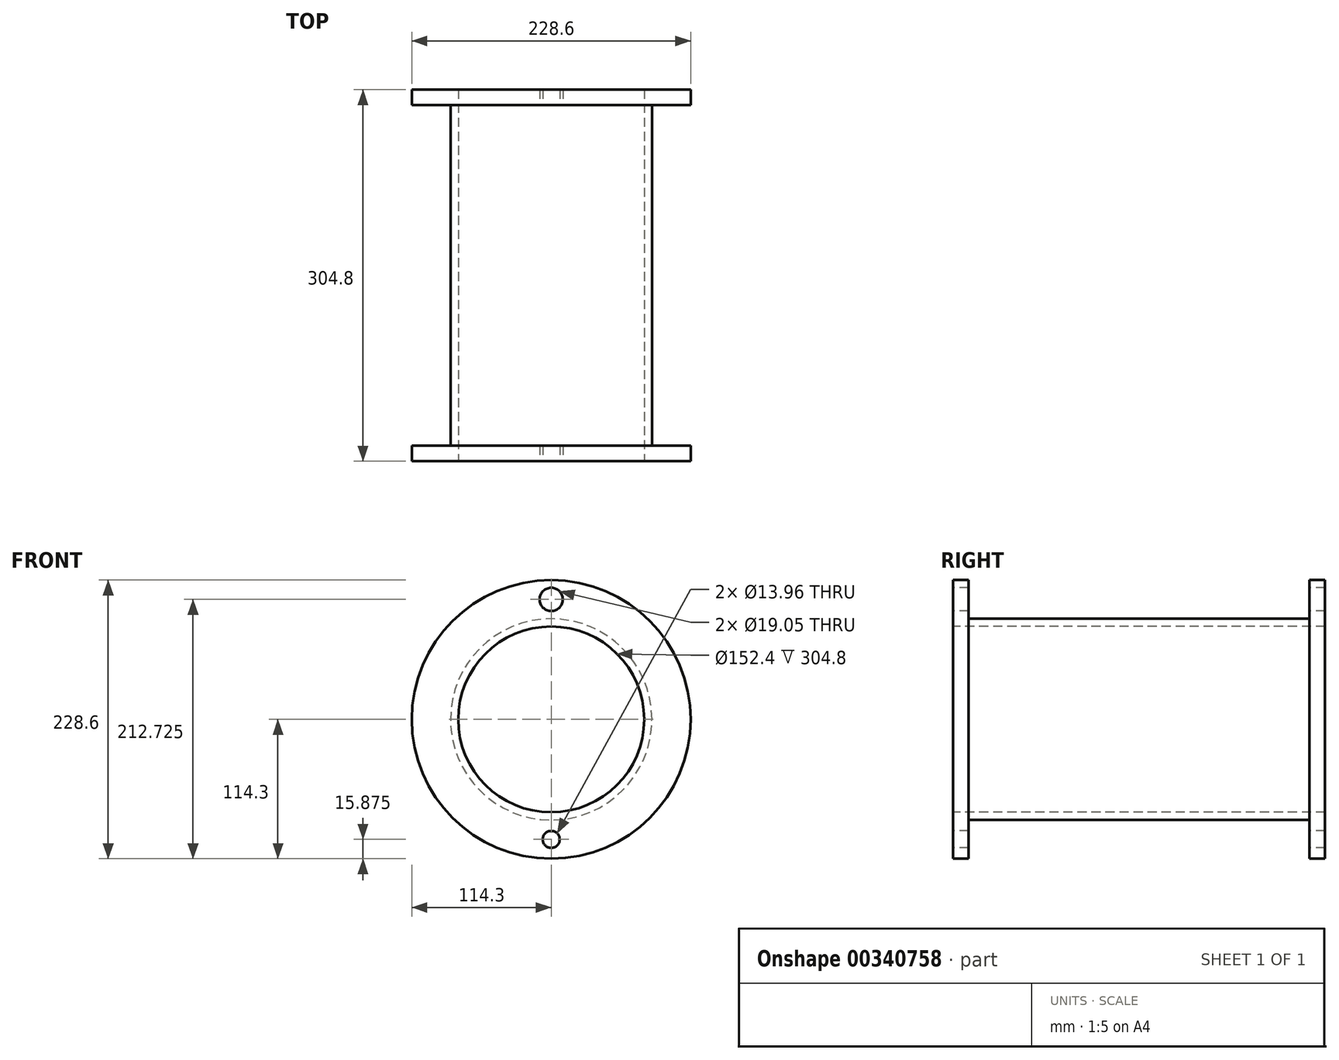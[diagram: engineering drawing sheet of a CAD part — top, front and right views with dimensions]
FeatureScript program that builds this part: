
annotation { "Feature Type Name" : "Feature", "Feature Type Description" : "" }
export const myFeature = defineFeature(function(context is Context, id is Id, definition is map)
    precondition{}
    {
        {
            var Q0;
            Q0=qCreatedBy(makeId("Right.planeOp"),FACE);
            var sketch = newSketch(context, id + "F0", { "sketchPlane" : qUnion([Q0])});
            skLineSegment(sketch, "E0", {"start": v(-372.41, 0) * mm, "end": v(512.39, 0) * mm, "construction": true});
            skLineSegment(sketch, "E1", {"start": v(0, 114.3) * mm, "end": v(-12.7, 114.3) * mm});
            skLineSegment(sketch, "E2", {"start": v(-12.7, 114.3) * mm, "end": v(-12.7, 82.55) * mm});
            skLineSegment(sketch, "E3", {"start": v(-12.7, 82.55) * mm, "end": v(-292.1, 82.55) * mm});
            skLineSegment(sketch, "E4", {"start": v(-292.1, 82.55) * mm, "end": v(-292.1, 114.3) * mm});
            skLineSegment(sketch, "E5", {"start": v(-292.1, 114.3) * mm, "end": v(-304.8, 114.3) * mm});
            skLineSegment(sketch, "E6", {"start": v(-304.8, 76.2) * mm, "end": v(0, 76.2) * mm});
            skLineSegment(sketch, "E7", {"start": v(-304.8, 114.3) * mm, "end": v(-304.8, 76.2) * mm});
            skLineSegment(sketch, "E8", {"start": v(0, 114.3) * mm, "end": v(0, 76.2) * mm});
            skSolve(sketch);
        }
        {
            var Q0;
            Q0=makeQuery(id+"F0.imprint","IMPRINT",FACE,{"disambiguationData":[TD([[makeQuery(id+"F0.imprint","IMPRINT",EDGE,{"derivedFrom":sQuery(id+"F0.wireOp",EDGE,"E1")}),1.0]])]});
            var Q1;
            Q1=sQuery(id+"F0.wireOp",EDGE,"E0");
            revolve(context, id + "F1", {"entities" : qUnion([Q0]), "axis" : qUnion([Q1]), "revolveType" : RevolveType.FULL});
        }
        {
            var Q0;
            Q0=makeQuery(id+"F1.opRevolve","SWEPT_FACE",FACE,{"disambiguationData":[OSD([sQuery(id+"F0.wireOp",EDGE,"E7")])]});
            cPlane(context, id + "F2", {"entities" : qUnion([Q0]), "cplaneType" : CPlaneType.OFFSET, "offset" : 0 * mm, "width" : 152.4 * mm, "height" : 152.4 * mm});
        }
        {
            var Q0;
            Q0=qCreatedBy(id+"F2.planeOp",FACE);
            var sketch = newSketch(context, id + "F3", { "sketchPlane" : qUnion([Q0])});
            skCircle(sketch, "E9", {"center": v(0, 0) * mm, "radius": 98.43 * mm, "construction": true});
            skCircle(sketch, "E10", {"center": v(0, 98.43) * mm, "radius": 9.53 * mm, "construction": true});
            skCircle(sketch, "E11.1.0", {"center": v(-69.6, 69.6) * mm, "radius": 9.53 * mm, "construction": true});
            skCircle(sketch, "E11.2.0", {"center": v(-98.43, 0) * mm, "radius": 9.53 * mm, "construction": true});
            skCircle(sketch, "E11.3.0", {"center": v(-69.6, -69.6) * mm, "radius": 9.53 * mm, "construction": true});
            skCircle(sketch, "E11.4.0", {"center": v(0, -98.43) * mm, "radius": 9.53 * mm, "construction": true});
            skCircle(sketch, "E11.5.0", {"center": v(69.6, -69.6) * mm, "radius": 9.53 * mm, "construction": true});
            skCircle(sketch, "E11.6.0", {"center": v(98.43, 0) * mm, "radius": 9.53 * mm, "construction": true});
            skCircle(sketch, "E11.7.0", {"center": v(69.6, 69.6) * mm, "radius": 9.53 * mm, "construction": true});
            skCircle(sketch, "E12", {"center": v(0, 98.43) * mm, "radius": 9.53 * mm});
            skCircle(sketch, "E13", {"center": v(0, -98.43) * mm, "radius": 6.98 * mm});
            skSolve(sketch);
        }
        {
            var Q0;
            Q0=qSketchRegion(id+"F3",true);
            extrude(context, id + "F4", {"entities" : qUnion([Q0]), "operationType" : NewBodyOperationType.REMOVE, "endBound" : BoundingType.THROUGH_ALL, "oppositeDirection" : true, "depth" : 635 * mm});
        }
    });
